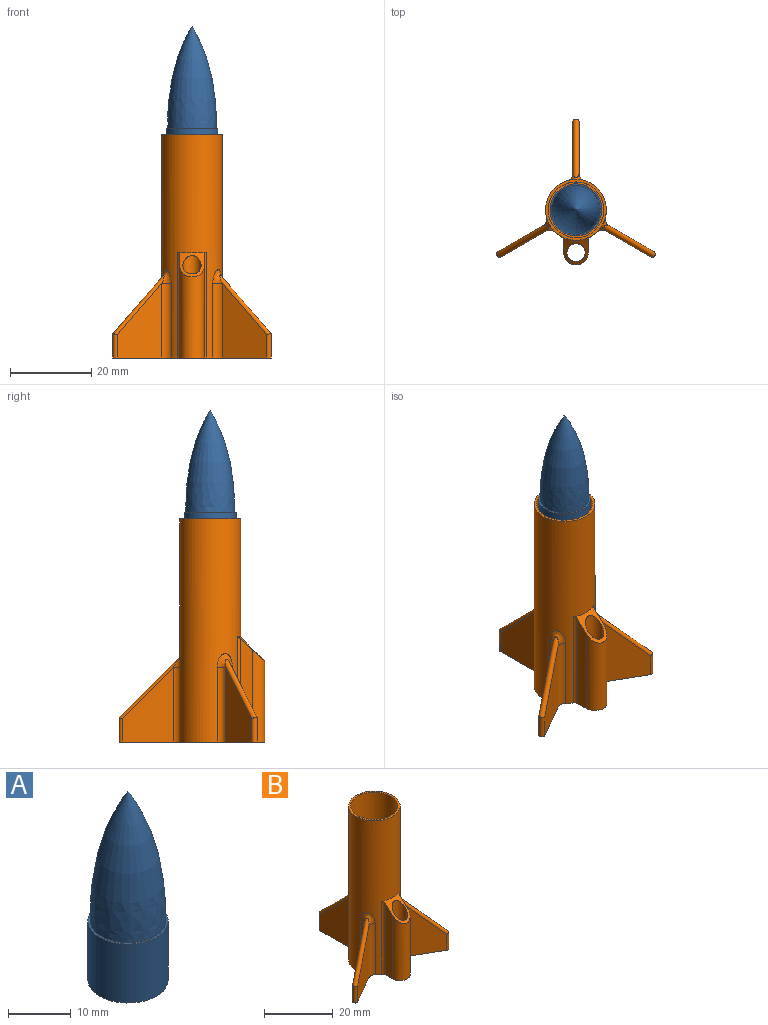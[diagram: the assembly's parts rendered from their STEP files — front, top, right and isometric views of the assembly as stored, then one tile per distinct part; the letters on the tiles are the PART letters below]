
ASSEMBLY  parts=2 mates=1
PART A: 7 faces, bbox 12.8x12.8x36.9 mm
  f0: plane 12.8x12.8mm, normal (0,0,-1), area 128.7mm2, adj f1
  f1: cylinder r=6.4mm len=12.8mm, axis (0,0,-1), area 462.4mm2, adj f0,f2
  f2: plane 12.8x12.8mm, normal (0,0,1), area 14.7mm2, adj f1,f3
  f3: revolved ~25.37x12.05mm, area 696mm2, adj f2
  f4: plane 9.8x9.8mm, normal (0,0,-1), area 75.4mm2, adj f5
  f5: cylinder r=4.9mm len=9.8mm, axis (0,0,-1), area 261.7mm2, adj f4,f6
  f6: plane 9.8x9.8mm, normal (0,0,1), area 75.4mm2, adj f5
PART B: 37 faces, bbox 39.3x36.1x55.2 mm
  f0: cylinder r=6.88mm len=35mm, axis (0,0,-1), area 1511.9mm2, adj f4,f24
  f1: cylinder r=7.5mm len=55mm, axis (0,0,-1), area 2120.3mm2, adj f3,f4,f21,f25,f26,f27,f28,f29
  f2: cylinder r=6.88mm len=13.75mm, axis (0,0,-1), area 561.6mm2, adj f3,f23
  f3: plane 15x15mm, normal (0,0,1), area 28.2mm2, adj f1,f2
  f4: plane 39.11x35.96mm, normal (0,0,-1), area 115.4mm2, adj f0,f1,f5,f6,f7,f9,f11,f12
  f5: plane 18.31x12.62mm, normal (1,0,0), area 151.4mm2, adj f4,f7,f8,f33
  f6: plane 18.31x12.62mm, normal (-1,0,0), area 151.4mm2, adj f4,f7,f8,f31
  f7: cylinder r=0.75mm len=5.69mm, axis (0,0,-1), area 13.4mm2, adj f4,f5,f6,f8
  f8: cylinder r=0.75mm len=14.69mm, axis (0,-0.71,0.71), area 45.5mm2, adj f5,f6,f7,f32
  f9: cylinder r=0.75mm len=5.69mm, axis (0,0,-1), area 13.4mm2, adj f4,f10,f11,f12
  f10: cylinder r=0.75mm len=14.69mm, axis (-0.61,0.35,0.71), area 45.5mm2, adj f9,f11,f12,f26
  f11: plane 18.31x10.93mm, normal (0.5,0.87,0), area 151.4mm2, adj f4,f9,f10,f27
  f12: plane 18.31x10.93mm, normal (-0.5,-0.87,0), area 151.4mm2, adj f4,f9,f10,f25
  f13: cylinder r=2.25mm len=25.25mm, axis (0,0,-1), area 323.4mm2, adj f4,f21
  f14: cylinder r=3mm len=22.58mm, axis (0,0,-1), area 197mm2, adj f4,f15,f16,f21
  f15: plane 25.57x3.15mm, normal (1,0,0), area 72mm2, adj f4,f14,f21,f34
  f16: plane 25.57x3.15mm, normal (-1,0,0), area 72mm2, adj f4,f14,f21,f35
  f17: plane 18.31x10.93mm, normal (-0.5,0.87,0), area 151.4mm2, adj f4,f19,f20,f30
  f18: plane 18.31x10.93mm, normal (0.5,-0.87,0), area 151.4mm2, adj f4,f19,f20,f28
  f19: cylinder r=0.75mm len=5.69mm, axis (0,0,-1), area 13.4mm2, adj f4,f17,f18,f20
  f20: cylinder r=0.75mm len=14.69mm, axis (0.61,0.35,0.71), area 45.5mm2, adj f17,f18,f19,f29
  f21: cone r=7.5mm half-angle=45deg, axis (0,0,-1), area 25.6mm2, adj f1,f13,f14,f15,f16,f34,f35
  f22: cylinder r=5.5mm len=11mm, axis (0,0,-1), area 200.5mm2, adj f23,f24,f36
  f23: plane 13.75x13.75mm, normal (0,0,1), area 53.5mm2, adj f2,f22
  f24: cone r=6.88mm half-angle=50.2deg, axis (0,0,-1), area 69.6mm2, adj f0,f22
  f25: cylinder r=2mm len=18.31mm, axis (0,0,-1), area 46.8mm2, adj f1,f4,f12,f26
  f26: bspline ~4.13x3.76mm, area 12.6mm2, adj f1,f10,f25,f27
  f27: cylinder r=2mm len=18.31mm, axis (0,0,-1), area 46.8mm2, adj f1,f4,f11,f26
  f28: cylinder r=2mm len=18.31mm, axis (0,0,-1), area 46.8mm2, adj f1,f4,f18,f29
  f29: bspline ~4.13x3.76mm, area 12.6mm2, adj f1,f20,f28,f30
  f30: cylinder r=2mm len=18.31mm, axis (0,0,-1), area 46.8mm2, adj f1,f4,f17,f29
  f31: cylinder r=2mm len=18.31mm, axis (0,0,-1), area 46.8mm2, adj f1,f4,f6,f32
  f32: bspline ~4.34x4.13mm, area 12.6mm2, adj f1,f8,f31,f33
  f33: cylinder r=2mm len=18.31mm, axis (0,0,-1), area 46.8mm2, adj f1,f4,f5,f32
  f34: cylinder r=1mm len=26mm, axis (0,0,-1), area 27.8mm2, adj f1,f4,f15,f21
  f35: cylinder r=1mm len=26mm, axis (0,0,-1), area 27.8mm2, adj f1,f4,f16,f21
  f36: cylinder r=0.75mm len=2mm, axis (0,-1,0), area 9.4mm2, adj f1,f22
PLACE A t=(-5.96,3.76,45.11)mm
PLACE B t=(-5.96,3.76,-9.89)mm fixed
MATE fastened B.f1 <-> A.f1  axis (0,0,1) through (-5.96,3.76,45.11)mm
